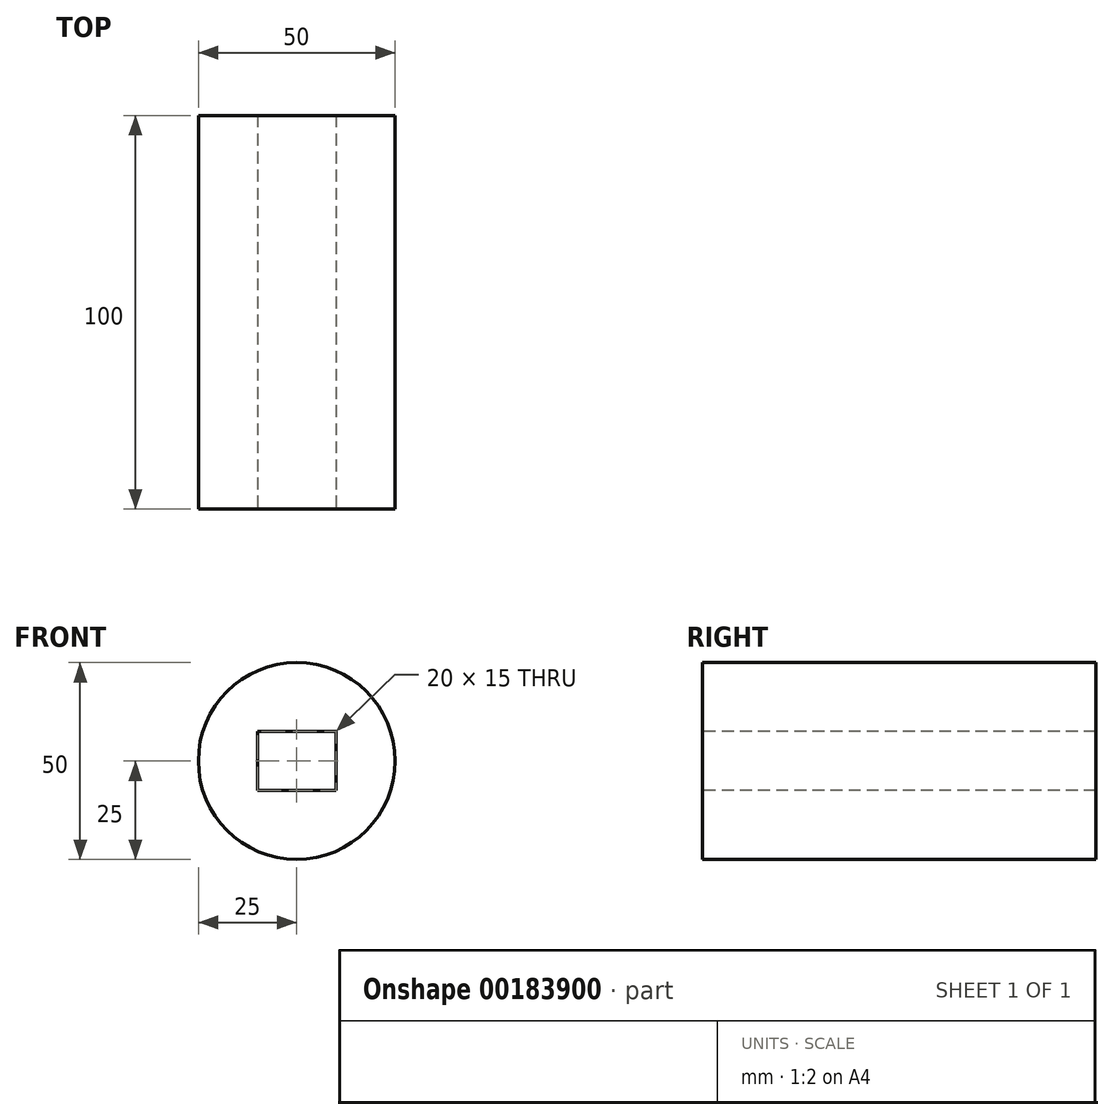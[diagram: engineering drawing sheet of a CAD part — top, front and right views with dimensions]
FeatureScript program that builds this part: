
annotation { "Feature Type Name" : "Feature", "Feature Type Description" : "" }
export const myFeature = defineFeature(function(context is Context, id is Id, definition is map)
    precondition{}
    {
        {
            var Q0;
            Q0=qCreatedBy(makeId("Front.planeOp"),FACE);
            var sketch = newSketch(context, id + "F0", { "sketchPlane" : qUnion([Q0])});
            skCircle(sketch, "E0", {"center": v(0, 0) * mm, "radius": 25 * mm});
            skSolve(sketch);
        }
        {
            var Q0;
            Q0 = qSketchRegion(id + "F0", true);
            extrude(context, id + "F1", {"entities" : qUnion([Q0]), "endBound" : BoundingType.SYMMETRIC, "depth" : 100 * mm});
        }
        {
            var Q0;
            Q0=qCreatedBy(makeId("Front.planeOp"),FACE);
            var sketch = newSketch(context, id + "F2", { "sketchPlane" : qUnion([Q0])});
            skLineSegment(sketch, "E1.bottom", {"start": v(10, 7.5) * mm, "end": v(-10, 7.5) * mm});
            skLineSegment(sketch, "E1.top", {"start": v(10, -7.5) * mm, "end": v(-10, -7.5) * mm});
            skLineSegment(sketch, "E1.left", {"start": v(10, 7.5) * mm, "end": v(10, -7.5) * mm});
            skLineSegment(sketch, "E1.right", {"start": v(-10, 7.5) * mm, "end": v(-10, -7.5) * mm});
            skPoint(sketch, "E1.middle", {"position": v(0, 0) * mm});
            skSolve(sketch);
        }
        {
            var Q0;
            Q0 = qSketchRegion(id + "F2", true);
            extrude(context, id + "F3", {"entities" : qUnion([Q0]), "operationType" : NewBodyOperationType.REMOVE, "endBound" : BoundingType.SYMMETRIC, "oppositeDirection" : true, "depth" : 120 * mm});
        }
    });
